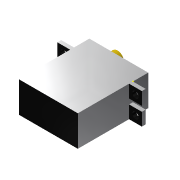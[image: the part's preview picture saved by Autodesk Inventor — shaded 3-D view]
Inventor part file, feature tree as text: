
AUTODESK INVENTOR PART (.ipt)
format: ipt  version: 2018 (Build 220112000, 112)  size: 195,072 bytes
history: native  units: mm
features: sketch x7, extrude x6, other x1
ambient origin geometry x8: Origin, YZ Plane, XZ Plane, XY Plane, X Axis, Y Axis, Z Axis, Center Point
bodies: Body1 (feature_tree)
feature tree (14):
  other  "Sólido1"
  extrude  "Extrusión1"  Depth=12.0mm
  extrude  "Extrusión2"  Depth=27.5mm
  extrude  "Extrusión3"  Depth=5.0mm
  extrude  "Extrusión4"  Depth=5.0mm
  extrude  "Extrusión5"  Depth=7.5mm
  extrude  "Extrusión6"  Depth=5.0mm
  sketch  "Sketch7"  dims[d15=5.0mm d16=5.0mm d17=28.0mm d18=0.0mm d19=0.0mm d20=2.5mm d21=2.5mm d22=2.5mm d23=2.5mm d24=5.0mm d25=0.0mm d26=10.5mm d27=3.0mm d28=4.5mm d29=6.0mm d30=5.0mm d31=0.0mm]
  sketch  "Boceto1"  dims[d0=23.0mm d1=12.0mm]
  sketch  "Boceto2"  dims[d2=27.5mm d3=0.0mm d4=17.0mm]
  sketch  "Boceto3"  dims[d5=8.5mm d6=5.0mm]
  sketch  "Boceto4"  dims[d7=5.0mm d8=0.0mm d9=8.5mm]
  sketch  "Boceto5"  dims[d10=1.5mm d11=0.0mm d12=7.5mm]
  sketch  "Boceto6"  dims[d13=1.5mm d14=5.0mm]
